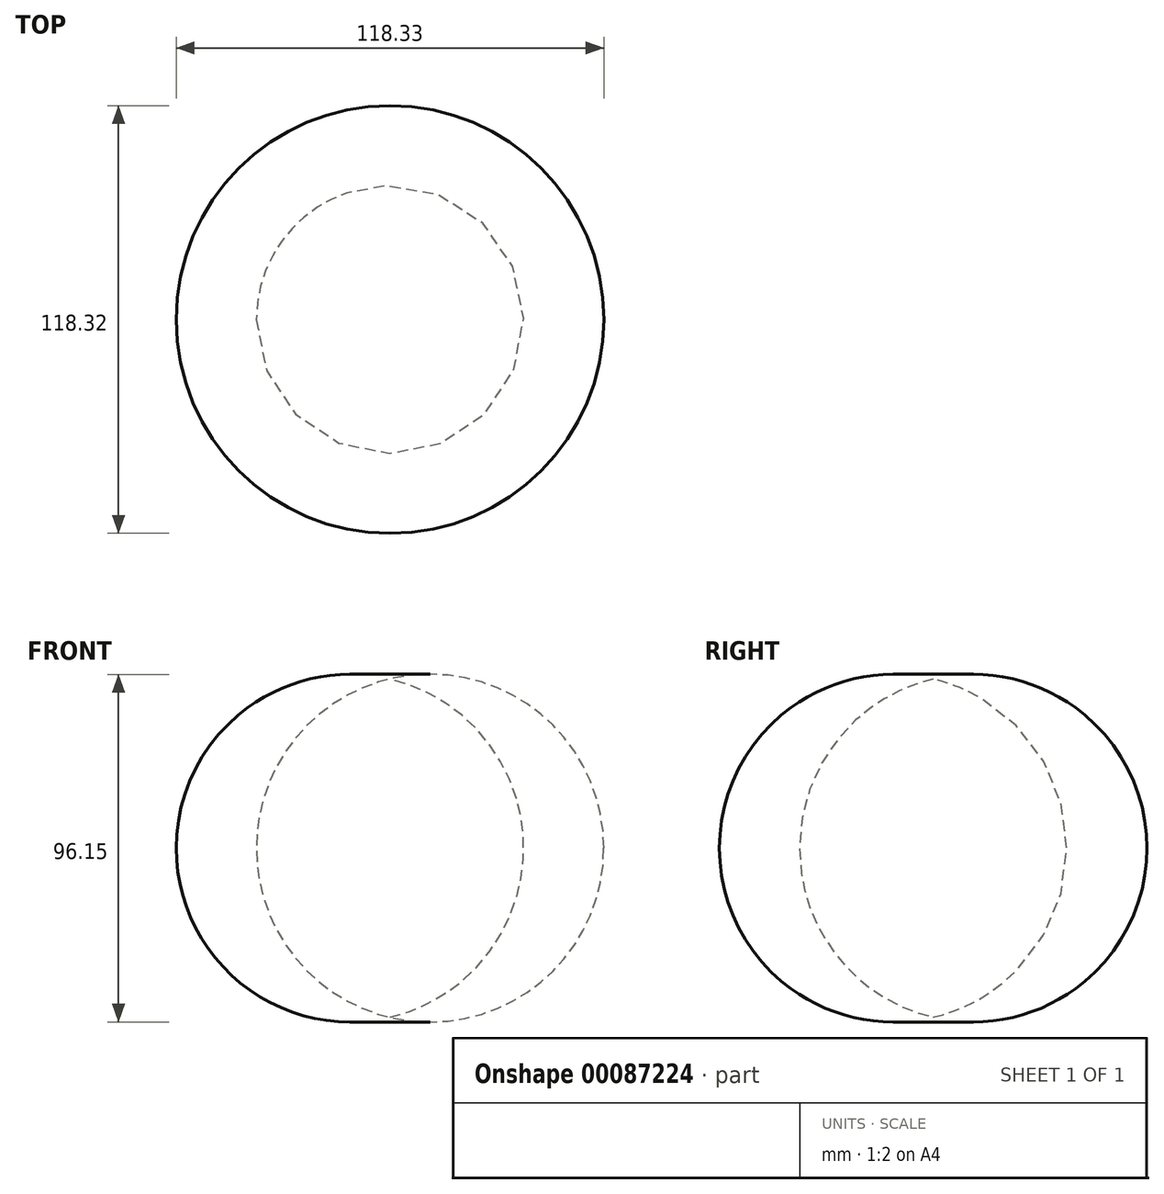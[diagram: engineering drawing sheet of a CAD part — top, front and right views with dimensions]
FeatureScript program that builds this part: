
annotation { "Feature Type Name" : "Feature", "Feature Type Description" : "" }
export const myFeature = defineFeature(function(context is Context, id is Id, definition is map)
    precondition{}
    {
        {
            var Q0;
            Q0=qCreatedBy(makeId("Front.planeOp"),FACE);
            var sketch = newSketch(context, id + "F0", { "sketchPlane" : qUnion([Q0])});
            skLineSegment(sketch, "E0", {"start": v(-45, 46.04) * mm, "end": v(-45, -47.53) * mm});
            skArc(sketch, "E1", {"start": v(-45, -47.53) * mm, "mid": v(14.17, -0.74) * mm, "end": v(-45, 46.04) * mm});
            skSolve(sketch);
        }
        {
            var Q0;
            Q0=makeQuery(id+"F0.imprint","IMPRINT",FACE,{"disambiguationData":[TD([[makeQuery(id+"F0.imprint","IMPRINT",EDGE,{"derivedFrom":sQuery(id+"F0.wireOp",EDGE,"E0")}),1.0]])]});
            var sketch = newSketch(context, id + "F1", { "sketchPlane" : qUnion([Q0])});
            skSolve(sketch);
        }
        {
            var Q0;
            Q0 = qSketchRegion(id + "F1", true);
            var Q1;
            Q1=makeQuery(id+"F0.imprint","IMPRINT",FACE,{"disambiguationData":[TD([[makeQuery(id+"F0.imprint","IMPRINT",EDGE,{"derivedFrom":sQuery(id+"F0.wireOp",EDGE,"E0")}),1.0]])]});
            var Q2;
            Q2=sQuery(id+"F0.wireOp",EDGE,"E0");
            revolve(context, id + "F2", {"entities" : qUnion([Q0, Q1]), "axis" : qUnion([Q2]), "revolveType" : RevolveType.FULL});
        }
    });
